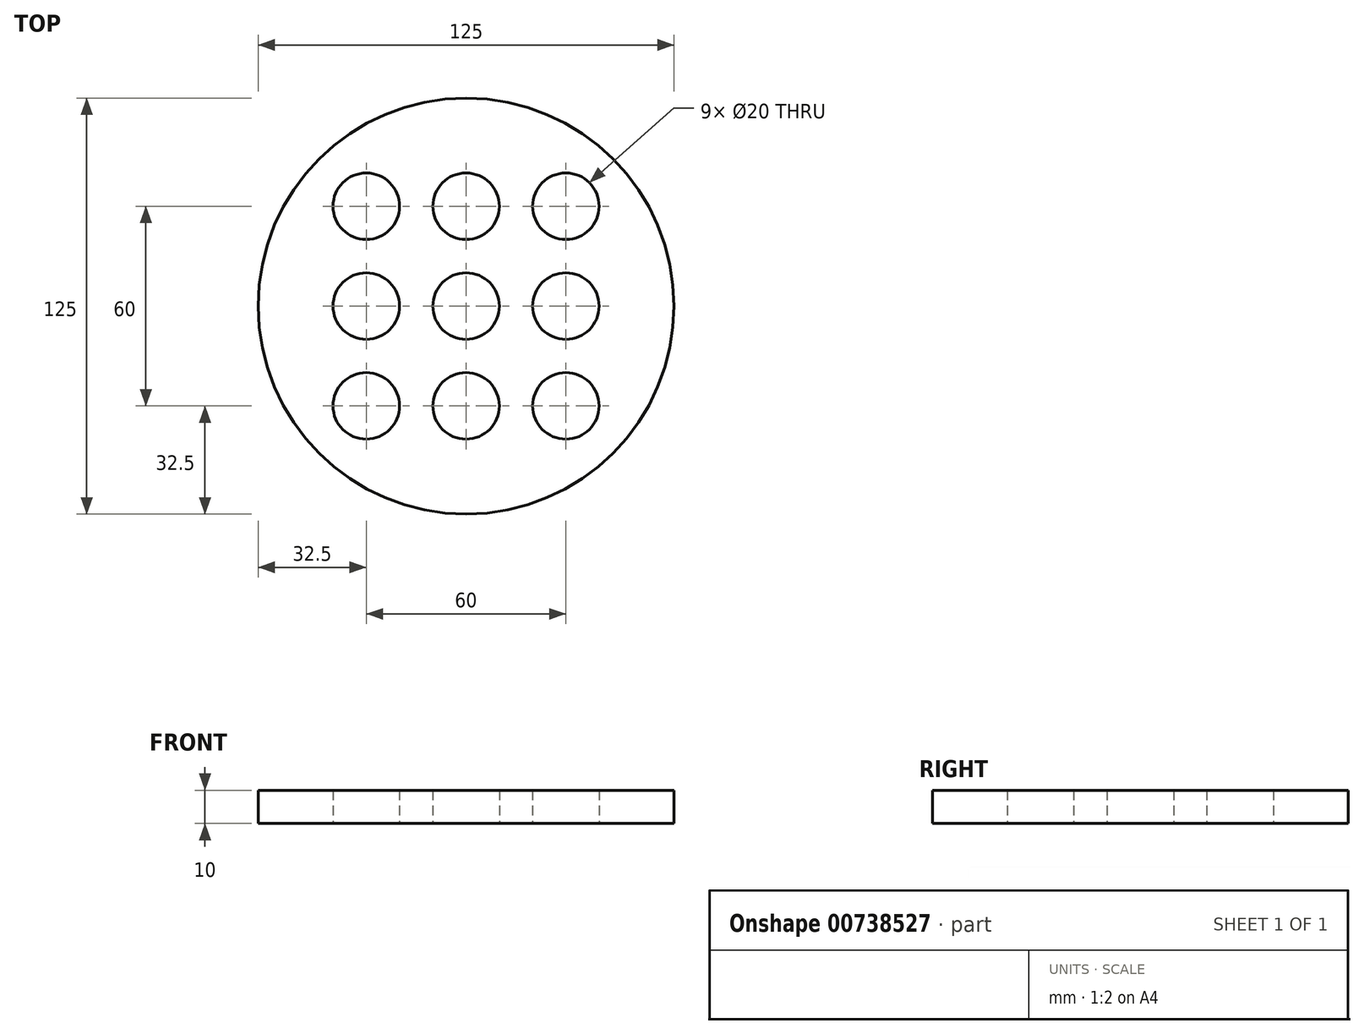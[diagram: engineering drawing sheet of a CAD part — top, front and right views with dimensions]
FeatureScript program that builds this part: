
annotation { "Feature Type Name" : "Feature", "Feature Type Description" : "" }
export const myFeature = defineFeature(function(context is Context, id is Id, definition is map)
    precondition{}
    {
        {
            var Q0;
            Q0=qCreatedBy(makeId("Top.planeOp"),FACE);
            var sketch = newSketch(context, id + "F0", { "sketchPlane" : qUnion([Q0])});
            skCircle(sketch, "E0", {"center": v(0, 0) * mm, "radius": 62.5 * mm});
            skCircle(sketch, "E1", {"center": v(0, 0) * mm, "radius": 10 * mm});
            skCircle(sketch, "E2", {"center": v(0, 30) * mm, "radius": 10 * mm});
            skCircle(sketch, "E3", {"center": v(-30, 0) * mm, "radius": 10 * mm});
            skCircle(sketch, "E4", {"center": v(-30, 30) * mm, "radius": 10 * mm});
            skCircle(sketch, "E5", {"center": v(30, 30) * mm, "radius": 10 * mm});
            skCircle(sketch, "E6", {"center": v(30, 0) * mm, "radius": 10 * mm});
            skCircle(sketch, "E7", {"center": v(30, -30) * mm, "radius": 10 * mm});
            skCircle(sketch, "E8", {"center": v(0, -30) * mm, "radius": 10 * mm});
            skCircle(sketch, "E9", {"center": v(-30, -30) * mm, "radius": 10 * mm});
            skSolve(sketch);
        }
        {
            var Q0;
            Q0=makeQuery(id+"F0.imprint","IMPRINT",FACE,{"disambiguationData":[TD([[makeQuery(id+"F0.imprint","IMPRINT",EDGE,{"derivedFrom":sQuery(id+"F0.wireOp",EDGE,"E0")}),1.0]])]});
            extrude(context, id + "F1", {"entities" : qUnion([Q0]), "depth" : 10 * mm, "offsetDistance" : 25 * mm});
        }
    });
